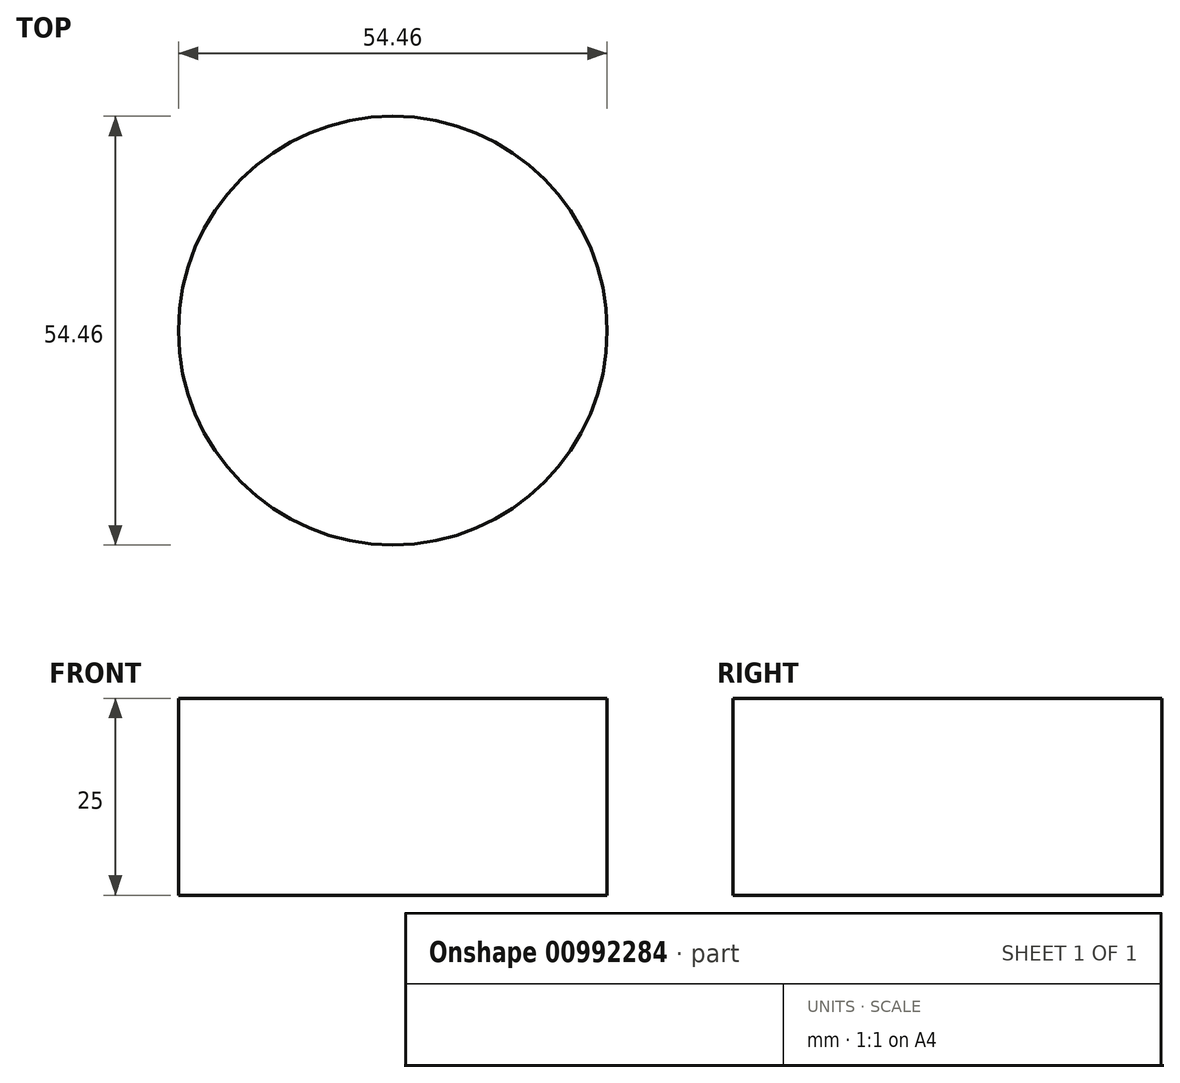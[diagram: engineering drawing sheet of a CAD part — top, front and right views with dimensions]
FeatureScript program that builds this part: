
annotation { "Feature Type Name" : "Feature", "Feature Type Description" : "" }
export const myFeature = defineFeature(function(context is Context, id is Id, definition is map)
    precondition{}
    {
        {
            var Q0;
            Q0=qCreatedBy(makeId("Top.planeOp"),FACE);
            var sketch = newSketch(context, id + "F0", { "sketchPlane" : qUnion([Q0])});
            skCircle(sketch, "E0", {"center": v(0, 0) * mm, "radius": 27.23 * mm});
            skSolve(sketch);
        }
        {
            var Q0;
            Q0 = qSketchRegion(id + "F0", true);
            var Q1;
            Q1=makeQuery(id+"F0.imprint","IMPRINT",FACE,{"disambiguationData":[TD([[makeQuery(id+"F0.imprint","IMPRINT",EDGE,{"derivedFrom":sQuery(id+"F0.wireOp",EDGE,"E0")}),1.0]])]});
            extrude(context, id + "F1", {"entities" : qUnion([Q0, Q1]), "depth" : 25 * mm, "offsetDistance" : 25 * mm});
        }
    });
